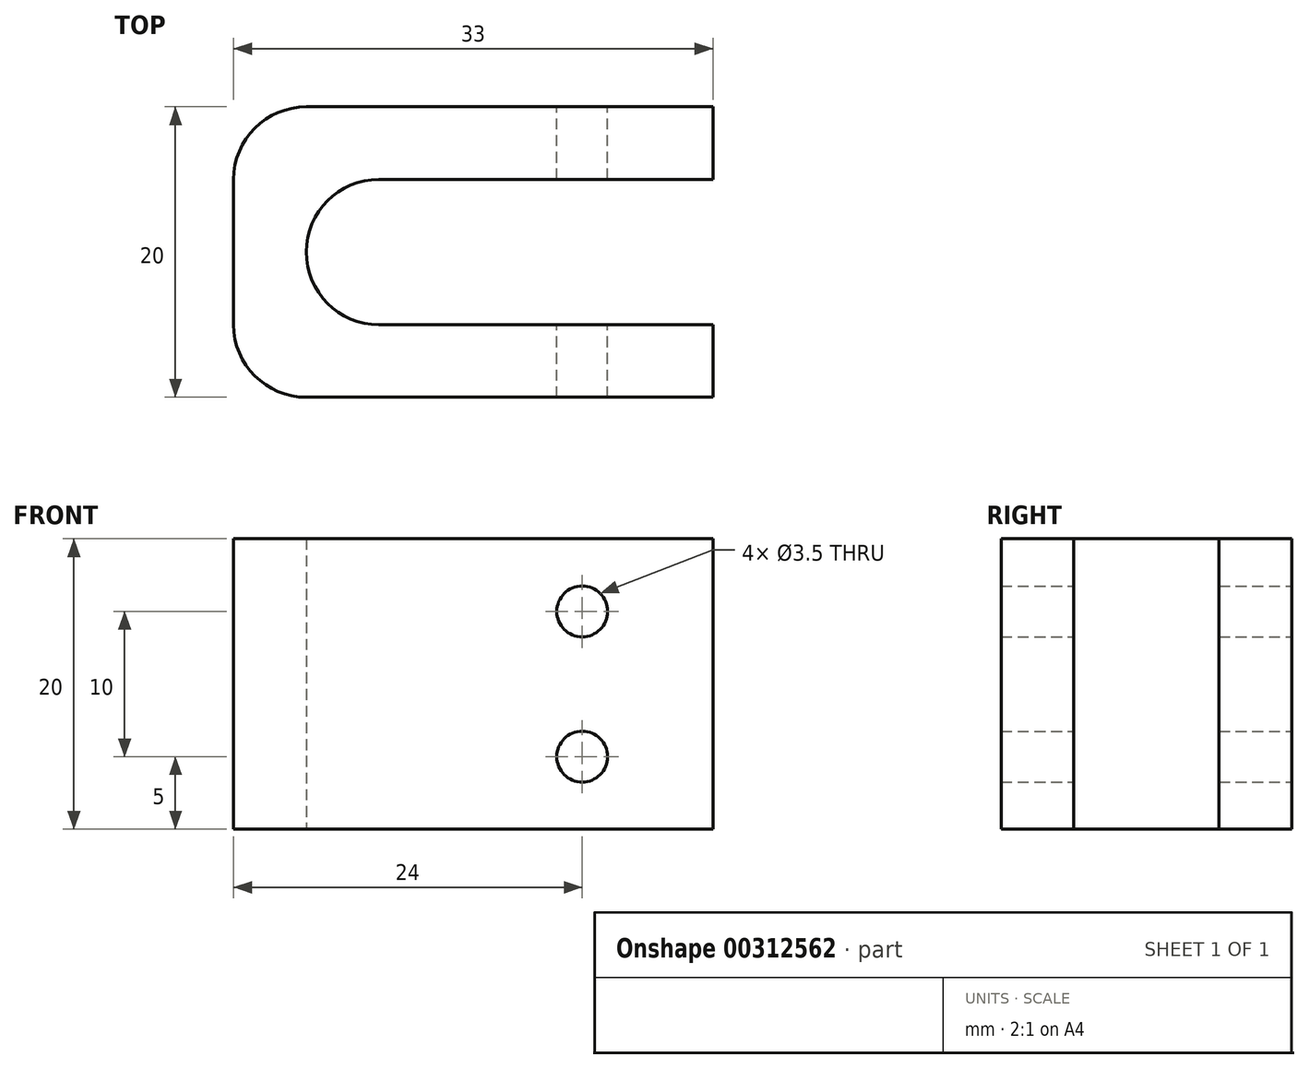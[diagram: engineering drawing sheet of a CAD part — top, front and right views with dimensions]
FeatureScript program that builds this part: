
annotation { "Feature Type Name" : "Feature", "Feature Type Description" : "" }
export const myFeature = defineFeature(function(context is Context, id is Id, definition is map)
    precondition{}
    {
        {
            var Q0;
            Q0=qCreatedBy(makeId("Top.planeOp"),FACE);
            var sketch = newSketch(context, id + "F0", { "sketchPlane" : qUnion([Q0])});
            skLineSegment(sketch, "E0.bottom", {"start": v(-16.5, 10) * mm, "end": v(16.5, 10) * mm});
            skLineSegment(sketch, "E0.top", {"start": v(-16.5, -10) * mm, "end": v(16.5, -10) * mm});
            skLineSegment(sketch, "E0.left", {"start": v(-16.5, 10) * mm, "end": v(-16.5, -10) * mm});
            skLineSegment(sketch, "E0.right", {"start": v(16.5, 10) * mm, "end": v(16.5, -10) * mm});
            skPoint(sketch, "E0.middle", {"position": v(0, 0) * mm});
            skCircle(sketch, "E1", {"center": v(-6.5, 0) * mm, "radius": 5 * mm});
            skLineSegment(sketch, "E2.bottom", {"start": v(-6.5, -5) * mm, "end": v(16.5, -5) * mm});
            skLineSegment(sketch, "E2.top", {"start": v(-6.5, 5) * mm, "end": v(16.5, 5) * mm});
            skLineSegment(sketch, "E2.right", {"start": v(16.5, -5) * mm, "end": v(16.5, 5) * mm});
            skSolve(sketch);
        }
        {
            var Q0;
            {var subQ1=sQuery(id+"F0.wireOp",EDGE,"E0.bottom");Q0=makeQuery(id+"F0.imprint","IMPRINT",FACE,{"disambiguationData":[TD([[makeQuery(id+"F0.imprint","IMPRINT",EDGE,{"derivedFrom":subQ1}),-1.0]])]});}
            extrude(context, id + "F1", {"entities" : qUnion([Q0]), "depth" : 20 * mm});
        }
        {
            var Q0;
            Q0=qCreatedBy(makeId("Front.planeOp"),FACE);
            var sketch = newSketch(context, id + "F2", { "sketchPlane" : qUnion([Q0])});
            skCircle(sketch, "E3", {"center": v(7.5, 15) * mm, "radius": 1.75 * mm});
            skCircle(sketch, "E4", {"center": v(7.5, 5) * mm, "radius": 1.75 * mm});
            skSolve(sketch);
        }
        {
            var Q0;
            Q0 = qSketchRegion(id + "F2", true);
            extrude(context, id + "F3", {"entities" : qUnion([Q0]), "operationType" : NewBodyOperationType.REMOVE, "depth" : 25 * mm, "symmetric" : true});
        }
        {
            var Q0;
            Q0=makeQuery(id+"F1.opExtrude","SWEPT_EDGE",EDGE,{"disambiguationData":[OSD([sQuery(id+"F0.wireOp",EDGE,"E0.bottom"),sQuery(id+"F0.wireOp",EDGE,"E0.left")])]});
            var Q1;
            Q1=makeQuery(id+"F1.opExtrude","SWEPT_EDGE",EDGE,{"disambiguationData":[OSD([sQuery(id+"F0.wireOp",EDGE,"E0.top"),sQuery(id+"F0.wireOp",EDGE,"E0.left")])]});
            fillet(context, id + "F4", {"entities" : qUnion([Q0, Q1]), "radius" : 5 * mm, "tangentPropagation" : true, "allowEdgeOverflow" : false});
        }
    });
